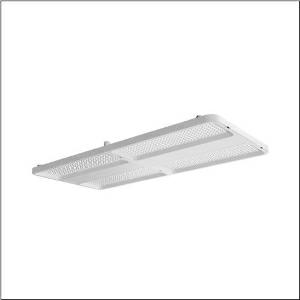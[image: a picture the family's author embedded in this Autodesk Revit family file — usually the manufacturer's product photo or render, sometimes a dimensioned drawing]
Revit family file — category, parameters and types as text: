
# Revit family: highbay_21_maxi_52hn12db3lda
name_source: partatom
category: Lighting Fixtures
units: mm (PartAtom-declared; Revit-internal decimal feet)

## family parameters
Cut with Voids When Loaded = No
Host = Face
Light Source = No
Part Type = Normal
Room Calculation Point = No
Round Connector Dimension = Use Diameter
Shared = No

## types (1)
- --- (1 x LED, 3880 lm, 22.6 W, 3000K)
    Apparent Load = 23 VA
    CIE Flux Codes = 90 98 100 100 100
    Color Rendering = 80
    Color Temperature = 3000K
    Default Elevation = 1800 mm
    Description = high bay luminaire Highbay 21 maxi; direct symmetric wide distribution, light control with lens of PMMA; UGR ≤ 22 (X = 4H | Y = 8H | S = 0.25H | reflection values 70/50/20); luminous flux: 25.590lm; light colour: 830, colour temperature: 3000K, MacAdam ≤ 3 SDCM (initial), colour rendering: CRI > 80; luminous efficacy: 177,7lm/W; rated service life: 75.000h (L80/B50) at AT= ta max; control: DALI 2; luminaire connection: terminal, 5-pole, max. 2.5mm² (cable entry for one cable, Ø 8.5..16mm); mains connection: 230..240V, AC/DC 0/50..60Hz; connected load: 144W; protection rating (complete): IP66; insulation class (complete): insulation class I (protective earthing); protection symbol: D; impact resistance: IK08; certification: CE, ENEC, VDE, UKCA; luminaire for central battery installations according to DIN EN 60598-2-22, internal wiring halogen-free; luminaire corresponds to IFS (International Featured Standards) requirements for safety and quality in the food industry; LABS conformity tested according to VDMA 24364:2018-05; housing frame of high-performance plastic PA6, matt traffic white (RAL 9016); cover of PMMA; dimension (LxWxH): 946 x 442 x 72mm; permissible operating ambient temperature: -40..+65°C (reducing of maximum allowable ambient temperature of 5°C with ceiling mounting); packaging unit: 1 piece; (delivery without accessories; please order mounting accessories separately)
    Height = 72 mm  [stored 0.23622 ft]
    Lamp = 1 x LED
    Lamp Light Flux = 3880 lm
    Lamp Power = 22.6 W
    Lamp count = 1
    Length = 946 mm
    Luminous efficacy = 172 lm/W
    Manufacturer = Siteco
    ModVariant = No
    Model = 52HN12DB3LDA
    Mounting Place = Ceiling
    Mounting Type = Pendant
    Number of Poles = 1
    OnlyDefault = Yes
    Power Factor = 1
    Product Name = Highbay 21 maxi
    Product group = high bay luminaire
    ProductGroupID = 901
    Protection Class = Protection class I
    Protection Degree = IP 66
    RLX_Detail_Level = 1
    RLX_Emergency_Light_Flux = 0 lm
    RLX_Emergency_Type = 0
    RLX_Emergency_Type_DB = No
    RlxData = <blob elided: 127989 chars, md5=75420810>
    Socket = socket
    Standby Power = 0 W
    System Light Flux = 3880 lm
    System Power = 23 W
    Type Comments = : DC mode (central or group accumulator) initial emergency light level
    Type Image = l_1363244.jpg
    URL = http://relux.com
    VarID = @adj_002591
    Voltage = 0 V
    Weight = 0.00 kg
    Width = 442 mm

note: [stored X ft] marks values corroborated as IEEE doubles in the binary element streams (Revit-internal decimal feet)

## geometry (parser evidence)
native form markers: Blend x4, Sweep x11
no freeform markers — native parametric forms only
